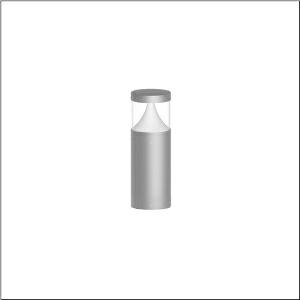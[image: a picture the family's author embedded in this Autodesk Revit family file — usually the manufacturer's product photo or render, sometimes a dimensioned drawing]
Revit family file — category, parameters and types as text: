
# Revit family: cl_31_poller_40_5cl424603
name_source: partatom
category: Lighting Fixtures
units: mm (PartAtom-declared; Revit-internal decimal feet)

## family parameters
Cut with Voids When Loaded = No
Host = Face
Light Source = No
Part Type = Normal
Room Calculation Point = No
Round Connector Dimension = Use Diameter
Shared = No

## types (1)
- --- (1 x LED, 800 lm, 7.2 W, 3000K)
    Apparent Load = 7 VA
    CIE Flux Codes = 19 66 88 92 100
    Color Rendering = 80
    Color Temperature = 3000K
    Default Elevation = 1800 mm
    Description = CL 31 Bollard 40, bollard luminaire, primary light control with lens, of PC, primary optical cover: cover panel, of PC, transparent, secondary light control with reflector, of PC, primary light characteristic: asymmetric, LED, rated luminous flux: 800lm, luminous efficacy: 110lm/W, light colour: 830, colour temperature: 3000K, control gear: ECG DALI, with terminal, 5-pole, max. 2.5mm², mains connection: 220..240V, AC, 50/60Hz, rated input power: 7.2W, luminaire housing, of aluminium, powder-coated, Siteco® metallic grey, diameter: 170mm, height: 400mm, protection rating (complete): IP65, insulation class (complete): insulation class I (protective earthing), certification: CE, ENEC, impact resistance: IK10, permissible operating ambient temperature for outdoor applications: -20..+50°C, packaging unit: 1 piece
    Height = 200 mm  [stored 0.656168 ft]
    Lamp = 1 x LED
    Lamp Light Flux = 800 lm
    Lamp Power = 7.2 W
    Lamp count = 1
    Length = 170 mm  [stored 0.557743 ft]
    Luminous efficacy = 111 lm/W
    Manufacturer = Siteco
    ModVariant = No
    Model = 5CL424603
    Mounting Place = Floor
    Mounting Type = Freestanding
    Number of Poles = 1
    OnlyDefault = Yes
    Power Factor = 1
    Product Name = CL 31 Poller 40
    Product group = bollard luminaire
    ProductGroupID = 1304
    Protection Class = Protection class I
    Protection Degree = IP 65
    RLX_Detail_Level = 1
    RLX_Emergency_Light_Flux = 0 lm
    RLX_Emergency_Type = 0
    RLX_Emergency_Type_DB = No
    RlxData = <blob elided: 62361 chars, md5=be8e3114>
    Socket = socket
    Standby Power = 0 W
    System Light Flux = 800 lm
    System Power = 7 W
    Type Comments = factory setting: luminous flux: 100 % | dim-lin: 254 | 182 mA
    Type Image = l_1006907.jpg
    URL = http://relux.com
    VarID = @adj_130407
    Voltage = 0 V
    Weight = 0.00 kg
    Width = 0 mm  [stored 0 ft]

note: [stored X ft] marks values corroborated as IEEE doubles in the binary element streams (Revit-internal decimal feet)

## geometry (parser evidence)
native form markers: Blend x4, Sweep x12
no freeform markers — native parametric forms only
